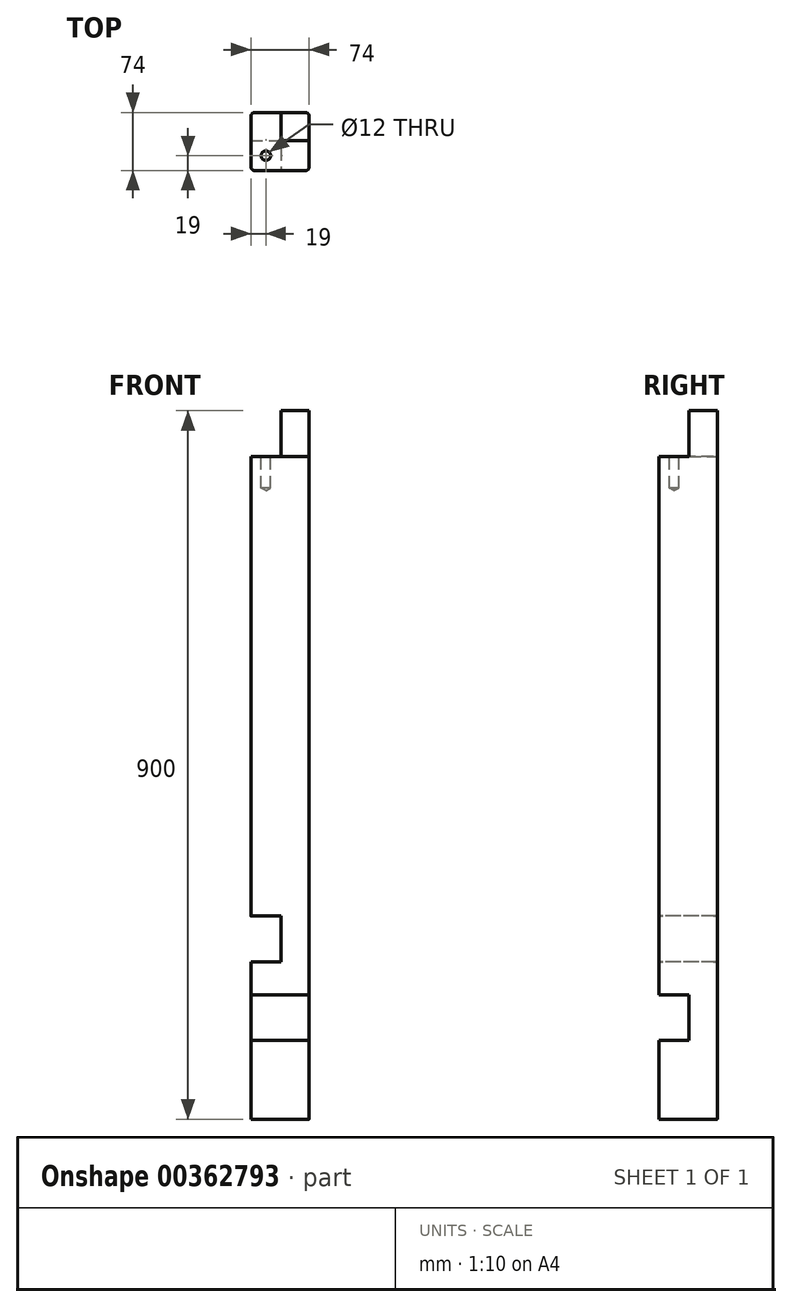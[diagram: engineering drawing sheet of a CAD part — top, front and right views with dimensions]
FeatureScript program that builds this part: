
annotation { "Feature Type Name" : "Feature", "Feature Type Description" : "" }
export const myFeature = defineFeature(function(context is Context, id is Id, definition is map)
    precondition{}
    {
        {
            var Q0;
            Q0=qCreatedBy(makeId("Top.planeOp"),FACE);
            var sketch = newSketch(context, id + "F0", { "sketchPlane" : qUnion([Q0])});
            skLineSegment(sketch, "E0.bottom", {"start": v(37, 37) * mm, "end": v(-37, 37) * mm});
            skLineSegment(sketch, "E0.top", {"start": v(37, -37) * mm, "end": v(-37, -37) * mm});
            skLineSegment(sketch, "E0.left", {"start": v(37, 37) * mm, "end": v(37, -37) * mm});
            skLineSegment(sketch, "E0.right", {"start": v(-37, 37) * mm, "end": v(-37, -37) * mm});
            skPoint(sketch, "E0.middle", {"position": v(0, 0) * mm});
            skSolve(sketch);
        }
        {
            var Q0;
            Q0=makeQuery(id+"F0.imprint","IMPRINT",FACE,{"disambiguationData":[TD([[makeQuery(id+"F0.imprint","IMPRINT",EDGE,{"derivedFrom":sQuery(id+"F0.wireOp",EDGE,"E0.bottom")}),1.0]])]});
            extrude(context, id + "F1", {"entities" : qUnion([Q0]), "oppositeDirection" : true, "depth" : 900 * mm});
        }
        {
            var Q0;
            Q0=makeQuery(id+"F1.opExtrude","SWEPT_FACE",FACE,{"disambiguationData":[OSD([sQuery(id+"F0.wireOp",EDGE,"E0.top")])]});
            var sketch = newSketch(context, id + "F2", { "sketchPlane" : qUnion([Q0])});
            skLineSegment(sketch, "E1", {"start": v(-37, -58) * mm, "end": v(37, -58) * mm});
            skSolve(sketch);
        }
        {
            var Q0;
            Q0=makeQuery(id+"F1.opExtrude","SWEPT_FACE",FACE,{"disambiguationData":[OSD([sQuery(id+"F0.wireOp",EDGE,"E0.right")])]});
            var sketch = newSketch(context, id + "F3", { "sketchPlane" : qUnion([Q0])});
            skLineSegment(sketch, "E2", {"start": v(37, -58) * mm, "end": v(-37, -58) * mm});
            skSolve(sketch);
        }
        {
            var Q0;
            {var subQ0=sQuery(id+"F2.wireOp",EDGE,"E1");Q0=makeQuery(id+"F2.imprint","IMPRINT",FACE,{"disambiguationData":[TD([[makeQuery(id+"F2.imprint","IMPRINT",EDGE,{"derivedFrom":subQ0}),1.0]])]});}
            extrude(context, id + "F4", {"entities" : qUnion([Q0]), "operationType" : NewBodyOperationType.REMOVE, "oppositeDirection" : true, "depth" : 38 * mm});
        }
        {
            var Q0;
            {var subQ0=sQuery(id+"F3.wireOp",EDGE,"E2");Q0=makeQuery(id+"F3.imprint","IMPRINT",FACE,{"disambiguationData":[TD([[makeQuery(id+"F3.imprint","IMPRINT",EDGE,{"derivedFrom":subQ0}),-1.0]])]});}
            extrude(context, id + "F5", {"entities" : qUnion([Q0]), "operationType" : NewBodyOperationType.REMOVE, "oppositeDirection" : true, "depth" : 38 * mm});
        }
        {
            var Q0;
            Q0=makeQuery(id+"F5.boolean.opBoolean","MERGE",FACE,{"derivedFrom":[makeQuery(id+"F4.boolean.opBoolean","COPY",FACE,{"derivedFrom":makeQuery(id+"F4.opExtrude","SWEPT_FACE",FACE,{"disambiguationData":[OSD([sQuery(id+"F2.wireOp",EDGE,"E1")])]})}),makeQuery(id+"F5.opExtrude","SWEPT_FACE",FACE,{"disambiguationData":[OSD([sQuery(id+"F3.wireOp",EDGE,"E2")])]})]});
            var sketch = newSketch(context, id + "F6", { "sketchPlane" : qUnion([Q0])});
            skPoint(sketch, "E3", {"position": v(-18, -18) * mm});
            skSolve(sketch);
        }
        {
            var Q0;
            Q0=sQuery(id+"F6.wireOp",VERTEX,"E3");
            var Q1;
            Q1=makeQuery(id+"F1.opExtrude","SWEPT_BODY",BODY,{"disambiguationData":[OSD([sQuery(id+"F0.wireOp",EDGE,"E0.bottom"),sQuery(id+"F0.wireOp",EDGE,"E0.top"),sQuery(id+"F0.wireOp",EDGE,"E0.left"),sQuery(id+"F0.wireOp",EDGE,"E0.right")])]});
            hole(context, id + "F7", {"style" : HoleStyle.SIMPLE, "endStyle" : HoleEndStyle.BLIND, "holeDiameter" : 12 * mm, "holeDepth" : 40 * mm, "isTappedThrough" : true, "tappedDepth" : 12 * mm, "tapClearance" : 3, "locations" : qUnion([Q0]), "scope" : qUnion([Q1])});
        }
        {
            var Q0;
            Q0=makeQuery(id+"F1.opExtrude","SWEPT_FACE",FACE,{"disambiguationData":[OSD([sQuery(id+"F0.wireOp",EDGE,"E0.top")])]});
            var sketch = newSketch(context, id + "F8", { "sketchPlane" : qUnion([Q0])});
            skLineSegment(sketch, "E4", {"start": v(-37, -742) * mm, "end": v(37, -742) * mm});
            skLineSegment(sketch, "E5", {"start": v(-37, -800) * mm, "end": v(37, -800) * mm});
            skSolve(sketch);
        }
        {
            var Q0;
            {var subQ0=sQuery(id+"F8.wireOp",EDGE,"E4");Q0=makeQuery(id+"F8.imprint","IMPRINT",FACE,{"disambiguationData":[TD([[makeQuery(id+"F8.imprint","IMPRINT",EDGE,{"derivedFrom":subQ0}),-1.0]])]});}
            extrude(context, id + "F9", {"entities" : qUnion([Q0]), "operationType" : NewBodyOperationType.REMOVE, "oppositeDirection" : true, "depth" : 38 * mm});
        }
        {
            var Q0;
            Q0=makeQuery(id+"F1.opExtrude","SWEPT_FACE",FACE,{"disambiguationData":[OSD([sQuery(id+"F0.wireOp",EDGE,"E0.right")])]});
            var sketch = newSketch(context, id + "F10", { "sketchPlane" : qUnion([Q0])});
            skLineSegment(sketch, "E6", {"start": v(-37, -700) * mm, "end": v(37, -700) * mm});
            skLineSegment(sketch, "E7", {"start": v(-37, -642) * mm, "end": v(37, -642) * mm});
            skSolve(sketch);
        }
        {
            var Q0;
            {var subQ0=sQuery(id+"F10.wireOp",EDGE,"E6");Q0=makeQuery(id+"F10.imprint","IMPRINT",FACE,{"disambiguationData":[TD([[makeQuery(id+"F10.imprint","IMPRINT",EDGE,{"derivedFrom":subQ0}),1.0]])]});}
            extrude(context, id + "F11", {"entities" : qUnion([Q0]), "operationType" : NewBodyOperationType.REMOVE, "oppositeDirection" : true, "depth" : 38 * mm});
        }
        {
            var Q0;
            Q0=makeQuery(id+"F1.opExtrude","SWEPT_EDGE",EDGE,{"disambiguationData":[OSD([sQuery(id+"F0.wireOp",EDGE,"E0.top"),sQuery(id+"F0.wireOp",EDGE,"E0.right")])]});
            var Q1;
            Q1=makeQuery(id+"F1.opExtrude","SWEPT_EDGE",EDGE,{"disambiguationData":[OSD([sQuery(id+"F0.wireOp",EDGE,"E0.bottom"),sQuery(id+"F0.wireOp",EDGE,"E0.right")])]});
            var Q2;
            Q2=makeQuery(id+"F1.opExtrude","SWEPT_EDGE",EDGE,{"disambiguationData":[OSD([sQuery(id+"F0.wireOp",EDGE,"E0.top"),sQuery(id+"F0.wireOp",EDGE,"E0.left")])]});
            var Q3;
            Q3=makeQuery(id+"F1.opExtrude","SWEPT_EDGE",EDGE,{"disambiguationData":[OSD([sQuery(id+"F0.wireOp",EDGE,"E0.bottom"),sQuery(id+"F0.wireOp",EDGE,"E0.left")])]});
            fillet(context, id + "F12", {"entities" : qUnion([Q0, Q1, Q2, Q3]), "radius" : 5 * mm, "tangentPropagation" : true, "allowEdgeOverflow" : false});
        }
    });
